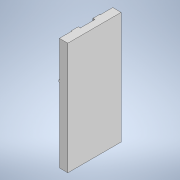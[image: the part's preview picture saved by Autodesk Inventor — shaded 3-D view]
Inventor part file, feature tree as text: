
AUTODESK INVENTOR PART (.ipt)
format: ipt  version: 2020.1 (Build 241239000, 239)  size: 137,216 bytes
history: native  units: mm
features: extrude x3, sketch x3, projected_geometry x3, other x1
ambient origin geometry x8: Origin, YZ Plane, XZ Plane, XY Plane, X Axis, Y Axis, Z Axis, Center Point
bodies: Body1 (feature_tree)
feature tree (10):
  other  "Твердое тело1"
  extrude  "Выдавливание1"  Depth=190.0mm
  extrude  "Выдавливание2"  Depth=30.0mm
  extrude  "Выдавливание3"  Depth=32.0mm
  sketch  "Эскиз1"
  sketch  "Эскиз2"
  projected_geometry  "Спроецированная петля1"
  sketch  "Эскиз3"
  projected_geometry  "Спроецированная петля2"
  projected_geometry  "Спроецированная петля3"
